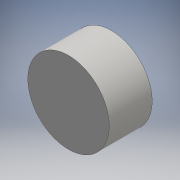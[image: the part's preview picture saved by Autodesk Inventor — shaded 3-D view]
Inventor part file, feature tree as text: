
AUTODESK INVENTOR PART (.ipt)
format: ipt  version: 2016 (Build 200138000, 138)  size: 90,624 bytes
history: native  units: mm
features: other x1, extrude x1, sketch x1
ambient origin geometry x8: Origin, YZ Plane, XZ Plane, XY Plane, X Axis, Y Axis, Z Axis, Center Point
bodies: Body1 (feature_tree)
feature tree (3):
  other  "Sólido1"
  extrude  "Extrusión1"  [1 undecoded]
  sketch  "Boceto3"  dims[d1=19.0mm d2=0.0mm]
note: 1 required parameter value undecoded (feature->parameter linkage not recoverable at this tier; creation-order binding heuristic only, values carry confidence <= 0.55)
